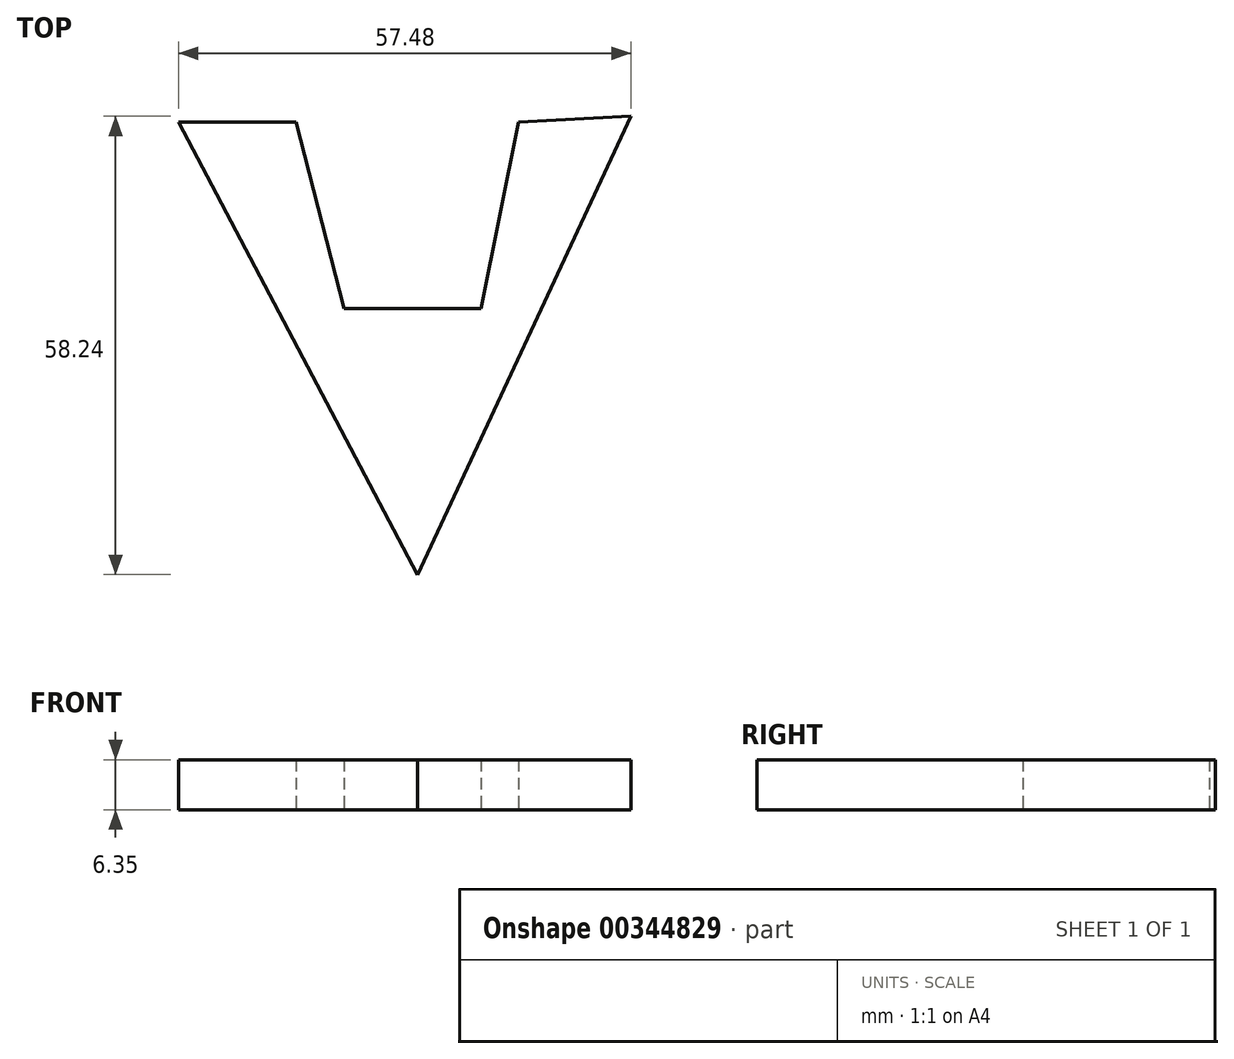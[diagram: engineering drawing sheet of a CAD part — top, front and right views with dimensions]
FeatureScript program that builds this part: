
annotation { "Feature Type Name" : "Feature", "Feature Type Description" : "" }
export const myFeature = defineFeature(function(context is Context, id is Id, definition is map)
    precondition{}
    {
        {
            var Q0;
            Q0=qCreatedBy(makeId("Top.planeOp"),FACE);
            var sketch = newSketch(context, id + "F0", { "sketchPlane" : qUnion([Q0])});
            skLineSegment(sketch, "E0", {"start": v(-63.59, 48.5) * mm, "end": v(-33.23, -8.97) * mm});
            skLineSegment(sketch, "E1", {"start": v(-33.23, -8.97) * mm, "end": v(-6.11, 49.27) * mm});
            skLineSegment(sketch, "E2", {"start": v(-63.59, 48.5) * mm, "end": v(-48.7, 48.5) * mm});
            skLineSegment(sketch, "E3", {"start": v(-6.11, 49.27) * mm, "end": v(-20.43, 48.5) * mm});
            skLineSegment(sketch, "E4", {"start": v(-48.7, 48.5) * mm, "end": v(-42.58, 24.82) * mm});
            skLineSegment(sketch, "E5", {"start": v(-20.43, 48.5) * mm, "end": v(-25.2, 24.82) * mm});
            skLineSegment(sketch, "E6", {"start": v(-42.58, 24.82) * mm, "end": v(-25.2, 24.82) * mm});
            skSolve(sketch);
        }
        {
            var Q0;
            Q0 = qSketchRegion(id + "F0", true);
            extrude(context, id + "F1", {"entities" : qUnion([Q0]), "depth" : 6.35 * mm});
        }
    });
